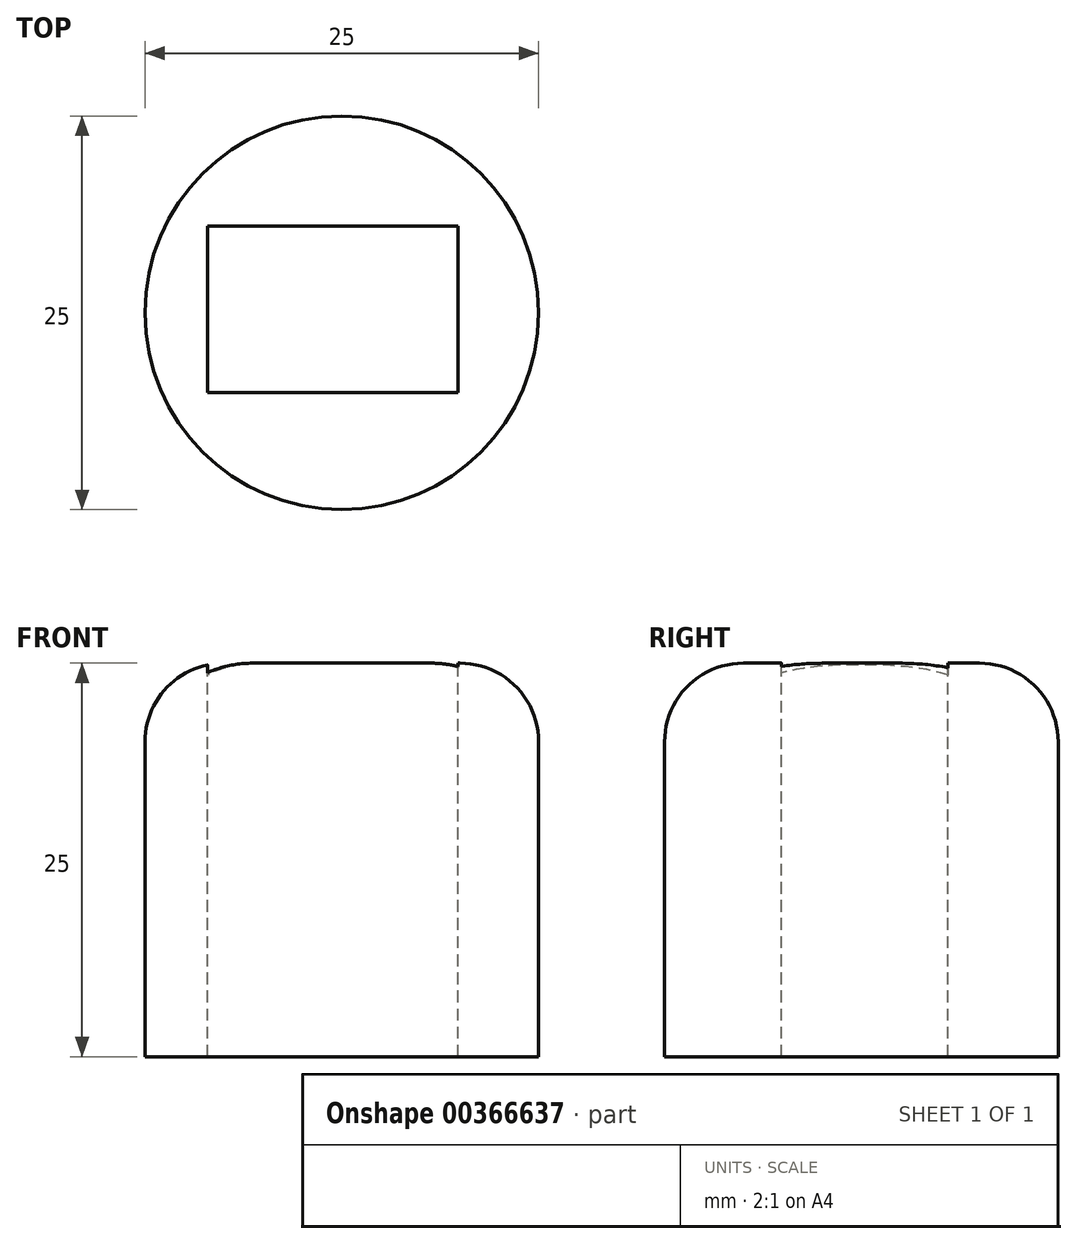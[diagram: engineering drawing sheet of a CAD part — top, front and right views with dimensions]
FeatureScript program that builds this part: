
annotation { "Feature Type Name" : "Feature", "Feature Type Description" : "" }
export const myFeature = defineFeature(function(context is Context, id is Id, definition is map)
    precondition{}
    {
        {
            var Q0;
            Q0=qCreatedBy(makeId("Top.planeOp"),FACE);
            var sketch = newSketch(context, id + "F0", { "sketchPlane" : qUnion([Q0])});
            skCircle(sketch, "E0", {"center": v(0, 0) * mm, "radius": 12.5 * mm});
            skSolve(sketch);
        }
        {
            var Q0;
            Q0=makeQuery(id+"F0.imprint","IMPRINT",FACE,{"disambiguationData":[TD([[makeQuery(id+"F0.imprint","IMPRINT",EDGE,{"derivedFrom":sQuery(id+"F0.wireOp",EDGE,"E0")}),1.0]])]});
            extrude(context, id + "F1", {"entities" : qUnion([Q0]), "depth" : 25 * mm});
        }
        {
            var Q0;
            Q0=makeQuery(id+"F1.opExtrude","CAP_FACE",FACE,{"disambiguationData":[OSD([sQuery(id+"F0.wireOp",EDGE,"E0")])],"isStart":false});
            var sketch = newSketch(context, id + "F2", { "sketchPlane" : qUnion([Q0])});
            skLineSegment(sketch, "E1.bottom", {"start": v(7.38, -5.06) * mm, "end": v(-8.54, -5.06) * mm});
            skLineSegment(sketch, "E1.top", {"start": v(7.38, 5.5) * mm, "end": v(-8.54, 5.5) * mm});
            skLineSegment(sketch, "E1.left", {"start": v(7.38, -5.06) * mm, "end": v(7.38, 5.5) * mm});
            skLineSegment(sketch, "E1.right", {"start": v(-8.54, -5.06) * mm, "end": v(-8.54, 5.5) * mm});
            skSolve(sketch);
        }
        {
            var Q0;
            Q0=makeQuery(id+"F2.imprint","IMPRINT",FACE,{"disambiguationData":[TD([[makeQuery(id+"F2.imprint","IMPRINT",EDGE,{"derivedFrom":sQuery(id+"F2.wireOp",EDGE,"E1.bottom")}),-1.0]])]});
            extrude(context, id + "F3", {"entities" : qUnion([Q0]), "operationType" : NewBodyOperationType.REMOVE, "oppositeDirection" : true, "depth" : 25 * mm});
        }
        {
            var Q0;
            Q0=makeQuery(id+"F1.opExtrude","CAP_EDGE",EDGE,{"disambiguationData":[OSD([sQuery(id+"F0.wireOp",EDGE,"E0")])],"isStart":false});
            fillet(context, id + "F4", {"entities" : qUnion([Q0]), "radius" : 5 * mm, "tangentPropagation" : true, "allowEdgeOverflow" : false});
        }
    });
